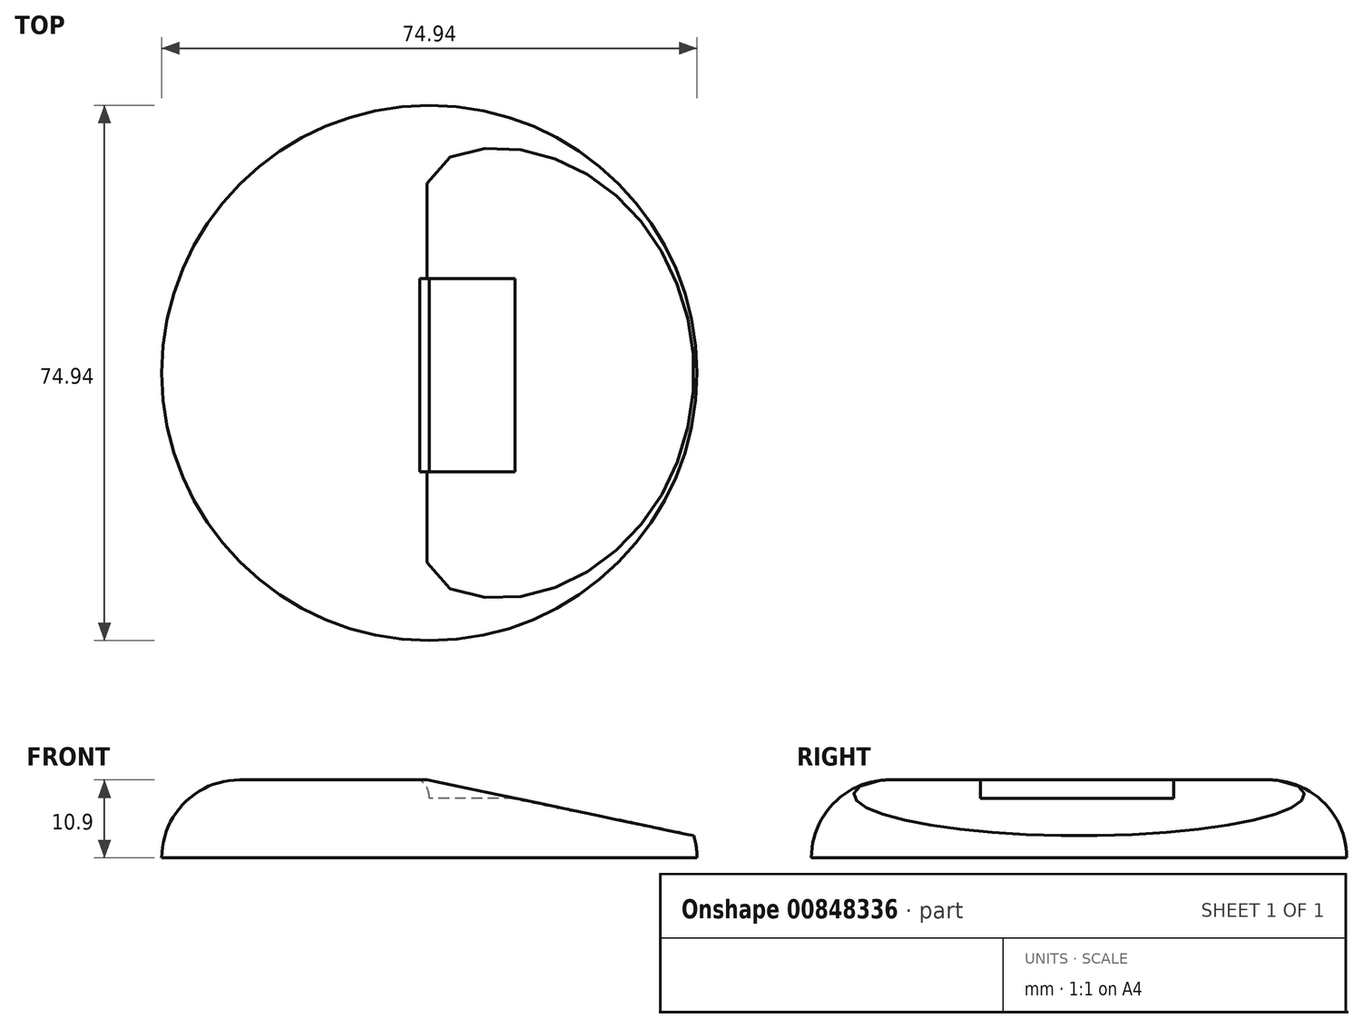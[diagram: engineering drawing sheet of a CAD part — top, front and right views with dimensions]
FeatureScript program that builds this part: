
annotation { "Feature Type Name" : "Feature", "Feature Type Description" : "" }
export const myFeature = defineFeature(function(context is Context, id is Id, definition is map)
    precondition{}
    {
        {
            var Q0;
            Q0=qCreatedBy(makeId("Front.planeOp"),FACE);
            var sketch = newSketch(context, id + "F0", { "sketchPlane" : qUnion([Q0])});
            skLineSegment(sketch, "E0", {"start": v(0, 0) * mm, "end": v(37.47, 0) * mm});
            skArc(sketch, "E1", {"start": v(37.47, 0) * mm, "mid": v(34.27, 7.71) * mm, "end": v(26.56, 10.9) * mm});
            skLineSegment(sketch, "E2", {"start": v(0, 0) * mm, "end": v(0, 10.9) * mm});
            skLineSegment(sketch, "E3", {"start": v(0, 10.9) * mm, "end": v(26.56, 10.9) * mm});
            skSolve(sketch);
        }
        {
            var Q0;
            Q0=makeQuery(id+"F0.imprint","IMPRINT",FACE,{"disambiguationData":[TD([[makeQuery(id+"F0.imprint","IMPRINT",EDGE,{"derivedFrom":sQuery(id+"F0.wireOp",EDGE,"E0")}),1.0]])]});
            var Q1;
            Q1=sQuery(id+"F0.wireOp",EDGE,"E2");
            revolve(context, id + "F1", {"surfaceOperationType" : NewSurfaceOperationType.NEW, "entities" : qUnion([Q0]), "axis" : qUnion([Q1]), "revolveType" : RevolveType.FULL});
        }
        {
            var Q0;
            Q0=qCreatedBy(makeId("Front.planeOp"),FACE);
            var sketch = newSketch(context, id + "F2", { "sketchPlane" : qUnion([Q0])});
            skLineSegment(sketch, "E4", {"start": v(-9.9, 12.92) * mm, "end": v(41.19, 2.2) * mm});
            skLineSegment(sketch, "E5", {"start": v(41.19, 2.2) * mm, "end": v(41.19, 15.2) * mm});
            skLineSegment(sketch, "E6", {"start": v(41.19, 15.2) * mm, "end": v(-10.25, 15.2) * mm});
            skLineSegment(sketch, "E7", {"start": v(-10.25, 15.2) * mm, "end": v(-9.9, 12.92) * mm});
            skSolve(sketch);
        }
        {
            var Q0;
            Q0 = qSketchRegion(id + "F2", true);
            extrude(context, id + "F3", {"entities" : qUnion([Q0]), "operationType" : NewBodyOperationType.REMOVE, "endBound" : BoundingType.THROUGH_ALL, "oppositeDirection" : true, "depth" : 40.4 * mm, "offsetDistance" : 25.4 * mm, "hasSecondDirection" : true, "secondDirectionBound" : SecondDirectionBoundingType.THROUGH_ALL, "secondDirectionOppositeDirection" : false, "secondDirectionDepth" : 46.74 * mm});
        }
        {
            var Q0;
            Q0=qCreatedBy(makeId("Right.planeOp"),FACE);
            var sketch = newSketch(context, id + "F4", { "sketchPlane" : qUnion([Q0])});
            skLineSegment(sketch, "E8.bottom", {"start": v(-13.82, 14.29) * mm, "end": v(13.25, 14.29) * mm});
            skLineSegment(sketch, "E8.top", {"start": v(-13.82, 8.33) * mm, "end": v(13.25, 8.33) * mm});
            skLineSegment(sketch, "E8.left", {"start": v(-13.82, 14.29) * mm, "end": v(-13.82, 8.33) * mm});
            skLineSegment(sketch, "E8.right", {"start": v(13.25, 14.29) * mm, "end": v(13.25, 8.33) * mm});
            skSolve(sketch);
        }
        {
            var Q0;
            Q0 = qSketchRegion(id + "F4", true);
            extrude(context, id + "F5", {"entities" : qUnion([Q0]), "operationType" : NewBodyOperationType.REMOVE, "endBound" : BoundingType.THROUGH_ALL, "depth" : 17.53 * mm, "offsetDistance" : 25.4 * mm});
        }
        {
            var Q0;
            Q0=makeQuery(id+"F5.boolean.opBoolean","INTERSECT",EDGE,{"derivedFrom":[makeQuery(id+"F3.boolean.opBoolean","COPY",FACE,{"derivedFrom":makeQuery(id+"F3.opExtrude","SWEPT_FACE",FACE,{"disambiguationData":[OSD([sQuery(id+"F2.wireOp",EDGE,"E4")])]})}),makeQuery(id+"F5.opExtrude","CAP_FACE",FACE,{"disambiguationData":[OSD([sQuery(id+"F4.wireOp",EDGE,"E8.bottom"),sQuery(id+"F4.wireOp",EDGE,"E8.top"),sQuery(id+"F4.wireOp",EDGE,"E8.left"),sQuery(id+"F4.wireOp",EDGE,"E8.right")])],"isStart":true})]});
            fillet(context, id + "F6", {"entities" : qUnion([Q0]), "radius" : 3 * mm, "tangentPropagation" : true, "allowEdgeOverflow" : false});
        }
    });
